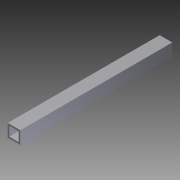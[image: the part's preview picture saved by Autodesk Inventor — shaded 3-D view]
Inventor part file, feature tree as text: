
AUTODESK INVENTOR PART (.ipt)
format: ipt  version: 2012 (Build 160160000, 160)  size: 76,800 bytes
history: native  units: in
note: dims shown in document units (in); Inventor stores cm internally (conversion verified against a paired STEP export)
features: extrude x1, sketch x1
ambient origin geometry x8: Origin, YZ Plane, XZ Plane, XY Plane, X Axis, Y Axis, Z Axis, Center Point
bodies: Solid1 (feature_tree)
feature tree (2):
  extrude  "Extrusion1"  Depth=1.0in
  sketch  "Sketch1"  dims[d0=1.0in d1=1.0in d2=0.125in d3=0.125in d4=0.125in d5=0.125in d6=12.0in d7=0.0in]
